# Revit family: Haworth_Planes_ConferenceTable_HalfRound
name_source: partatom
category: Furniture Systems
revit_build: Autodesk Revit 2018 (Build: 20170223_1515(x64)
units: mm (PartAtom-declared; Revit-internal decimal feet)

## family parameters
Always vertical = Yes
Cut with Voids When Loaded = No
OmniClass Number = 23.40.70.14.64.21
OmniClass Title = Systems Furniture
Part Type = Normal
Room Calculation Point = No
Round Connector Dimension = Use Diameter
Shared = No
Work Plane-Based = No

## types (2) — shared parameters
Actual Height = 29"
Assembly Code = E2020200
Cutout = Yes
Cutout Centerline = 9"
Cutout Depth = 4"
Cutout Width = 8"
Description = Haworth - Planes Conference Table - Half-Round
Edgeband = Yes
Flip Top = Yes
Flip Top Depth = 4 7/16"
Flip Top Finish = Haworth _ Paint _ Metallic Champagne
Flip Top Width = 8 5/16"
Knife Edge = No
Leg Height = 27 13/16"
Manufacturer = Haworth
Min/Max Depth = 30, 36 in.
Min/Max Width = 60, 72 in.
Model = TAHN
Opening Single = Yes
Opening Single Wide = No
Revision Number = 1
Size = Verify Final Dim. w/ Haworth
Support Spacing Back = 5"
Table Thickness = 1 3/16"
URL = www.haworth.com
URL - Product = https://www.haworth.com
Warranty = http://www.haworth.com

## per-type parameters (varying)
| type | Actual Depth | Actual Width | Large | Support Spacing Front | Sustainability Info |
| 72w 36d | 36" | 72" | Yes | 12" | https://www.haworth.com |
| 60w 30d | 30" | 60" | No | 9 1/2" | http://www.haworth.com |

## geometry (parser evidence)
native form markers: Sweep x11
no freeform markers — native parametric forms only
